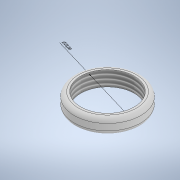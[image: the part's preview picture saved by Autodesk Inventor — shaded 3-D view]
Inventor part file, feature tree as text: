
AUTODESK INVENTOR PART (.ipt)
format: ipt  version: 2021 (Build 250183000, 183)  size: 152,576 bytes
history: native  units: mm
features: other x3, extrude x2, fillet x2, sketch x2
ambient origin geometry x8: Origin, YZ Plane, XZ Plane, XY Plane, X Axis, Y Axis, Z Axis, Center Point
bodies: Body1 (feature_tree)
feature tree (9):
  other  "Annotations"
  extrude  "Extrusion1"  Depth=31.0mm
  fillet  "Congé1"  Radius=7.0mm
  fillet  "Congé2"  Radius=2.0mm
  extrude  "Extrusion2"  Depth=2.0mm
  other  "Filetage3"
  sketch  "Esquisse1"
  sketch  "Esquisse3"
  other  "Cote de diamètre 1"
